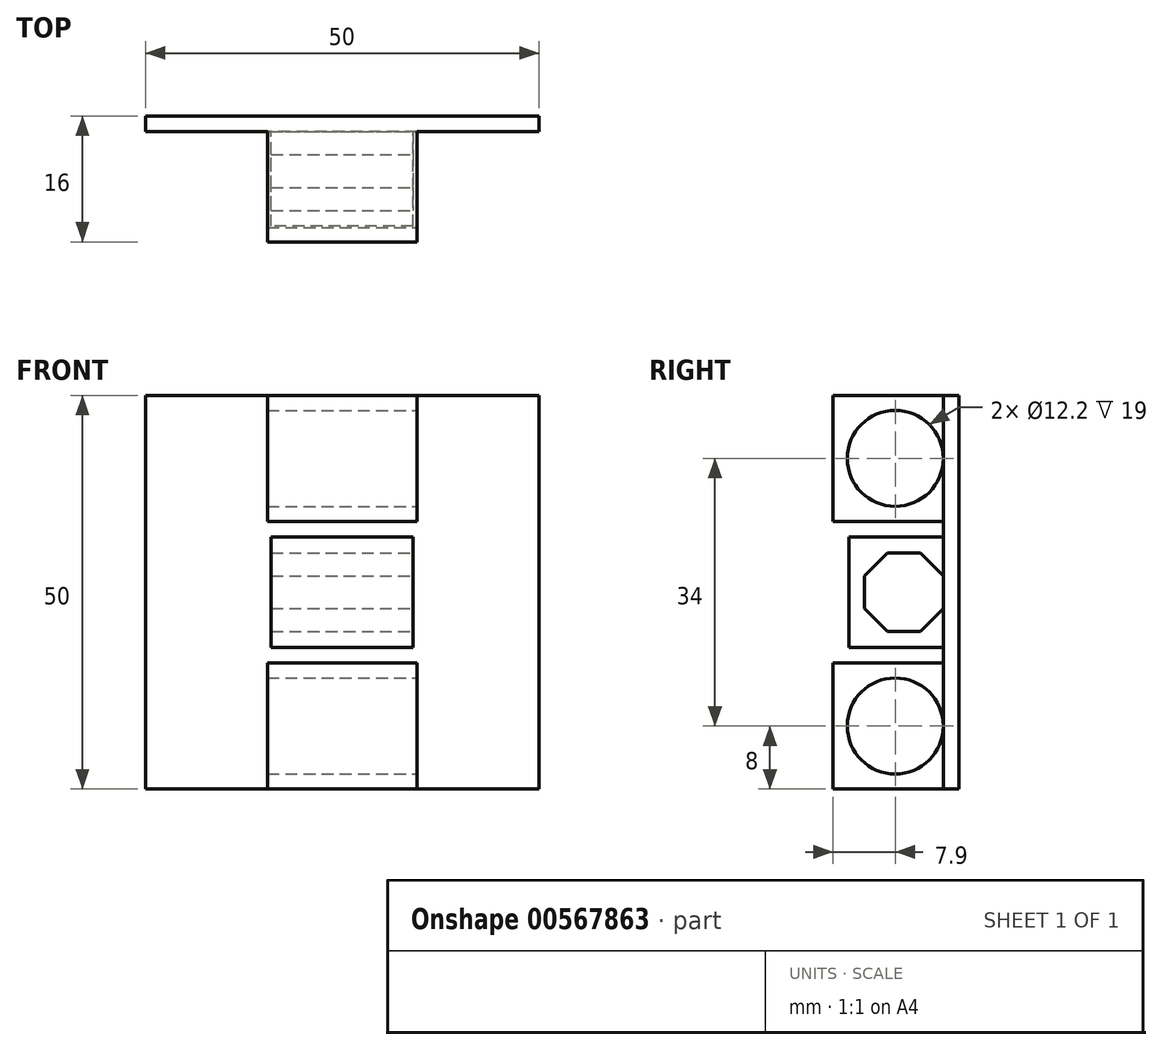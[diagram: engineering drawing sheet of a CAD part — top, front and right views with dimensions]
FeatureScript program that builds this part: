
annotation { "Feature Type Name" : "Feature", "Feature Type Description" : "" }
export const myFeature = defineFeature(function(context is Context, id is Id, definition is map)
    precondition{}
    {
        {
            var Q0;
            Q0=qCreatedBy(makeId("Front.planeOp"),FACE);
            var sketch = newSketch(context, id + "F0", { "sketchPlane" : qUnion([Q0])});
            skLineSegment(sketch, "E0.bottom", {"start": v(25, -25) * mm, "end": v(-25, -25) * mm});
            skLineSegment(sketch, "E0.top", {"start": v(25, 25) * mm, "end": v(-25, 25) * mm});
            skLineSegment(sketch, "E0.left", {"start": v(25, -25) * mm, "end": v(25, 25) * mm});
            skLineSegment(sketch, "E0.right", {"start": v(-25, -25) * mm, "end": v(-25, 25) * mm});
            skPoint(sketch, "E0.middle", {"position": v(0, 0) * mm});
            skLineSegment(sketch, "E1.bottom", {"start": v(-9.5, -9) * mm, "end": v(9.5, -9) * mm});
            skLineSegment(sketch, "E1.top", {"start": v(-9.5, -25) * mm, "end": v(9.5, -25) * mm});
            skLineSegment(sketch, "E1.left", {"start": v(-9.5, -9) * mm, "end": v(-9.5, -25) * mm});
            skLineSegment(sketch, "E1.right", {"start": v(9.5, -9) * mm, "end": v(9.5, -25) * mm});
            skPoint(sketch, "E1.middle", {"position": v(0, -17) * mm});
            skLineSegment(sketch, "E2.bottom", {"start": v(9.5, 9) * mm, "end": v(-9.5, 9) * mm});
            skLineSegment(sketch, "E2.top", {"start": v(9.5, 25) * mm, "end": v(-9.5, 25) * mm});
            skLineSegment(sketch, "E2.left", {"start": v(9.5, 9) * mm, "end": v(9.5, 25) * mm});
            skLineSegment(sketch, "E2.right", {"start": v(-9.5, 9) * mm, "end": v(-9.5, 25) * mm});
            skPoint(sketch, "E2.middle", {"position": v(0, 17) * mm});
            skLineSegment(sketch, "E3.bottom", {"start": v(9, -7) * mm, "end": v(-9, -7) * mm});
            skLineSegment(sketch, "E3.top", {"start": v(9, 7) * mm, "end": v(-9, 7) * mm});
            skLineSegment(sketch, "E3.left", {"start": v(9, -7) * mm, "end": v(9, 7) * mm});
            skLineSegment(sketch, "E3.right", {"start": v(-9, -7) * mm, "end": v(-9, 7) * mm});
            skSolve(sketch);
        }
        {
            var Q0;
            Q0 = qSketchRegion(id + "F0", true);
            extrude(context, id + "F1", {"entities" : qUnion([Q0]), "depth" : 2 * mm, "offsetDistance" : 25 * mm});
        }
        {
            var Q0;
            Q0=makeQuery(id+"F0.imprint","IMPRINT",FACE,{"disambiguationData":[TD([[makeQuery(id+"F0.imprint","IMPRINT",EDGE,{"derivedFrom":sQuery(id+"F0.wireOp",EDGE,"E3.bottom")}),-1.0]])]});
            extrude(context, id + "F2", {"entities" : qUnion([Q0]), "operationType" : NewBodyOperationType.ADD, "depth" : 14 * mm, "offsetDistance" : 25 * mm});
        }
        {
            var Q0;
            Q0=makeQuery(id+"F0.imprint","IMPRINT",FACE,{"disambiguationData":[TD([[makeQuery(id+"F0.imprint","IMPRINT",EDGE,{"derivedFrom":sQuery(id+"F0.wireOp",EDGE,"E1.bottom")}),-1.0]])]});
            var Q1;
            Q1=makeQuery(id+"F0.imprint","IMPRINT",FACE,{"disambiguationData":[TD([[makeQuery(id+"F0.imprint","IMPRINT",EDGE,{"derivedFrom":sQuery(id+"F0.wireOp",EDGE,"E2.bottom")}),-1.0]])]});
            extrude(context, id + "F3", {"entities" : qUnion([Q0, Q1]), "operationType" : NewBodyOperationType.ADD, "depth" : 16 * mm, "offsetDistance" : 25 * mm});
        }
        {
            var Q0;
            Q0=makeQuery(id+"F3.opExtrude","SWEPT_FACE",FACE,{"disambiguationData":[OSD([sQuery(id+"F0.wireOp",EDGE,"E1.right")])]});
            var sketch = newSketch(context, id + "F4", { "sketchPlane" : qUnion([Q0])});
            skCircle(sketch, "E4", {"center": v(-8.1, -17) * mm, "radius": 6.1 * mm});
            skSolve(sketch);
        }
        {
            var Q0;
            Q0=sQuery(id+"F4.wireOp",VERTEX,"E4.center");
            var Q1;
            Q1=makeQuery(id+"F1.opExtrude","SWEPT_BODY",BODY,{"disambiguationData":[OSD([sQuery(id+"F0.wireOp",EDGE,"E0.bottom"),sQuery(id+"F0.wireOp",EDGE,"E0.top"),sQuery(id+"F0.wireOp",EDGE,"E0.left"),sQuery(id+"F0.wireOp",EDGE,"E0.right"),sQuery(id+"F0.wireOp",EDGE,"E1.top"),sQuery(id+"F0.wireOp",EDGE,"E2.top"),sQuery(id+"F0.wireOp",EDGE,"E3.bottom"),sQuery(id+"F0.wireOp",EDGE,"E3.top"),sQuery(id+"F0.wireOp",EDGE,"E3.left"),sQuery(id+"F0.wireOp",EDGE,"E3.right")])]});
            hole(context, id + "F5", {"style" : HoleStyle.SIMPLE, "endStyle" : HoleEndStyle.THROUGH, "holeDiameter" : 12.2 * mm, "isTappedThrough" : true, "tappedDepth" : 12 * mm, "tapClearance" : 3, "locations" : qUnion([Q0]), "scope" : qUnion([Q1])});
        }
        {
            var Q0;
            Q0=makeQuery(id+"F3.opExtrude","SWEPT_FACE",FACE,{"disambiguationData":[OSD([sQuery(id+"F0.wireOp",EDGE,"E2.left")])]});
            var sketch = newSketch(context, id + "F6", { "sketchPlane" : qUnion([Q0])});
            skCircle(sketch, "E5", {"center": v(-8.1, 17) * mm, "radius": 6.1 * mm});
            skSolve(sketch);
        }
        {
            var Q0;
            Q0=sQuery(id+"F6.wireOp",VERTEX,"E5.center");
            var Q1;
            Q1=makeQuery(id+"F1.opExtrude","SWEPT_BODY",BODY,{"disambiguationData":[OSD([sQuery(id+"F0.wireOp",EDGE,"E0.bottom"),sQuery(id+"F0.wireOp",EDGE,"E0.top"),sQuery(id+"F0.wireOp",EDGE,"E0.left"),sQuery(id+"F0.wireOp",EDGE,"E0.right"),sQuery(id+"F0.wireOp",EDGE,"E1.top"),sQuery(id+"F0.wireOp",EDGE,"E2.top"),sQuery(id+"F0.wireOp",EDGE,"E3.bottom"),sQuery(id+"F0.wireOp",EDGE,"E3.top"),sQuery(id+"F0.wireOp",EDGE,"E3.left"),sQuery(id+"F0.wireOp",EDGE,"E3.right")])]});
            hole(context, id + "F7", {"style" : HoleStyle.SIMPLE, "endStyle" : HoleEndStyle.THROUGH, "holeDiameter" : 12.2 * mm, "isTappedThrough" : true, "tappedDepth" : 12 * mm, "tapClearance" : 3, "locations" : qUnion([Q0]), "scope" : qUnion([Q1])});
        }
        {
            var Q0;
            Q0=makeQuery(id+"F2.opExtrude","SWEPT_FACE",FACE,{"disambiguationData":[OSD([sQuery(id+"F0.wireOp",EDGE,"E3.left")])]});
            var sketch = newSketch(context, id + "F8", { "sketchPlane" : qUnion([Q0])});
            skLineSegment(sketch, "E6.bottom", {"start": v(0.07, 0) * mm, "end": v(-7, 7.07) * mm});
            skLineSegment(sketch, "E6.top", {"start": v(-7, -7.07) * mm, "end": v(-14.07, 0) * mm});
            skLineSegment(sketch, "E6.left", {"start": v(0.07, 0) * mm, "end": v(-7, -7.07) * mm});
            skLineSegment(sketch, "E6.right", {"start": v(-7, 7.07) * mm, "end": v(-14.07, 0) * mm});
            skPoint(sketch, "E6.middle", {"position": v(-7, 0) * mm});
            skCircle(sketch, "E7", {"center": v(-7, 0) * mm, "radius": 5 * mm});
            skLineSegment(sketch, "E8.bottom", {"start": v(-2, -5) * mm, "end": v(-12, -5) * mm});
            skLineSegment(sketch, "E8.top", {"start": v(-2, 5) * mm, "end": v(-12, 5) * mm});
            skLineSegment(sketch, "E8.left", {"start": v(-2, -5) * mm, "end": v(-2, 5) * mm});
            skLineSegment(sketch, "E8.right", {"start": v(-12, -5) * mm, "end": v(-12, 5) * mm});
            skSolve(sketch);
        }
        {
            var Q0;
            {var subQ0=sQuery(id+"F8.wireOp",EDGE,"E7");var subQ1=sQuery(id+"F8.wireOp",EDGE,"E6.top");var subQ2=makeQuery(id+"F8.imprint","INTERSECT",VERTEX,{"derivedFrom":[subQ1,subQ0]});Q0=makeQuery(id+"F8.imprint","IMPRINT",FACE,{"disambiguationData":[TD([[makeQuery(id+"F8.imprint","IMPRINT",EDGE,{"disambiguationData":[TD([[subQ2,-1.0]])],"derivedFrom":subQ1}),-1.0]])]});}
            var Q1;
            {var subQ0=sQuery(id+"F8.wireOp",EDGE,"E7");var subQ4=makeQuery(id+"F8.imprint","INTERSECT",VERTEX,{"derivedFrom":[sQuery(id+"F8.wireOp",EDGE,"E6.bottom"),subQ0]});Q1=makeQuery(id+"F8.imprint","IMPRINT",FACE,{"disambiguationData":[TD([[makeQuery(id+"F8.imprint","IMPRINT",EDGE,{"disambiguationData":[TD([[subQ4,1.0]])],"derivedFrom":subQ0}),1.0]])]});}
            var Q2;
            {var subQ0=sQuery(id+"F8.wireOp",EDGE,"E7");var subQ1=sQuery(id+"F8.wireOp",EDGE,"E6.right");var subQ2=makeQuery(id+"F8.imprint","INTERSECT",VERTEX,{"derivedFrom":[subQ1,subQ0]});Q2=makeQuery(id+"F8.imprint","IMPRINT",FACE,{"disambiguationData":[TD([[makeQuery(id+"F8.imprint","IMPRINT",EDGE,{"disambiguationData":[TD([[subQ2,-1.0]])],"derivedFrom":subQ1}),1.0]])]});}
            var Q3;
            {var subQ0=sQuery(id+"F8.wireOp",EDGE,"E8.top");var subQ1=sQuery(id+"F8.wireOp",EDGE,"E6.right");var subQ2=makeQuery(id+"F8.imprint","INTERSECT",VERTEX,{"derivedFrom":[subQ1,subQ0]});Q3=makeQuery(id+"F8.imprint","IMPRINT",FACE,{"disambiguationData":[TD([[makeQuery(id+"F8.imprint","IMPRINT",EDGE,{"disambiguationData":[TD([[subQ2,-1.0]])],"derivedFrom":subQ1}),1.0]])]});}
            var Q4;
            {var subQ0=sQuery(id+"F8.wireOp",EDGE,"E7");var subQ1=sQuery(id+"F8.wireOp",EDGE,"E6.bottom");var subQ2=makeQuery(id+"F8.imprint","INTERSECT",VERTEX,{"derivedFrom":[subQ1,subQ0]});Q4=makeQuery(id+"F8.imprint","IMPRINT",FACE,{"disambiguationData":[TD([[makeQuery(id+"F8.imprint","IMPRINT",EDGE,{"disambiguationData":[TD([[subQ2,-1.0]])],"derivedFrom":subQ1}),1.0]])]});}
            var Q5;
            {var subQ0=sQuery(id+"F8.wireOp",EDGE,"E8.left");var subQ1=sQuery(id+"F8.wireOp",EDGE,"E6.left");var subQ2=makeQuery(id+"F8.imprint","INTERSECT",VERTEX,{"derivedFrom":[subQ1,subQ0]});Q5=makeQuery(id+"F8.imprint","IMPRINT",FACE,{"disambiguationData":[TD([[makeQuery(id+"F8.imprint","IMPRINT",EDGE,{"disambiguationData":[TD([[subQ2,-1.0]])],"derivedFrom":subQ1}),-1.0]])]});}
            var Q6;
            {var subQ0=sQuery(id+"F8.wireOp",EDGE,"E8.left");var subQ1=sQuery(id+"F8.wireOp",EDGE,"E6.bottom");var subQ2=makeQuery(id+"F8.imprint","INTERSECT",VERTEX,{"derivedFrom":[subQ1,subQ0]});Q6=makeQuery(id+"F8.imprint","IMPRINT",FACE,{"disambiguationData":[TD([[makeQuery(id+"F8.imprint","IMPRINT",EDGE,{"disambiguationData":[TD([[subQ2,-1.0]])],"derivedFrom":subQ1}),1.0]])]});}
            var Q7;
            {var subQ0=sQuery(id+"F8.wireOp",EDGE,"E7");var subQ1=sQuery(id+"F8.wireOp",EDGE,"E6.left");var subQ2=makeQuery(id+"F8.imprint","INTERSECT",VERTEX,{"derivedFrom":[subQ1,subQ0]});Q7=makeQuery(id+"F8.imprint","IMPRINT",FACE,{"disambiguationData":[TD([[makeQuery(id+"F8.imprint","IMPRINT",EDGE,{"disambiguationData":[TD([[subQ2,-1.0]])],"derivedFrom":subQ1}),-1.0]])]});}
            var Q8;
            {var subQ0=sQuery(id+"F8.wireOp",EDGE,"E8.bottom");var subQ1=sQuery(id+"F8.wireOp",EDGE,"E6.top");var subQ2=makeQuery(id+"F8.imprint","INTERSECT",VERTEX,{"derivedFrom":[subQ1,subQ0]});Q8=makeQuery(id+"F8.imprint","IMPRINT",FACE,{"disambiguationData":[TD([[makeQuery(id+"F8.imprint","IMPRINT",EDGE,{"disambiguationData":[TD([[subQ2,-1.0]])],"derivedFrom":subQ1}),-1.0]])]});}
            extrude(context, id + "F9", {"entities" : qUnion([Q0, Q1, Q2, Q3, Q4, Q5, Q6, Q7, Q8]), "operationType" : NewBodyOperationType.REMOVE, "oppositeDirection" : true, "depth" : 25 * mm, "offsetDistance" : 25 * mm});
        }
    });
